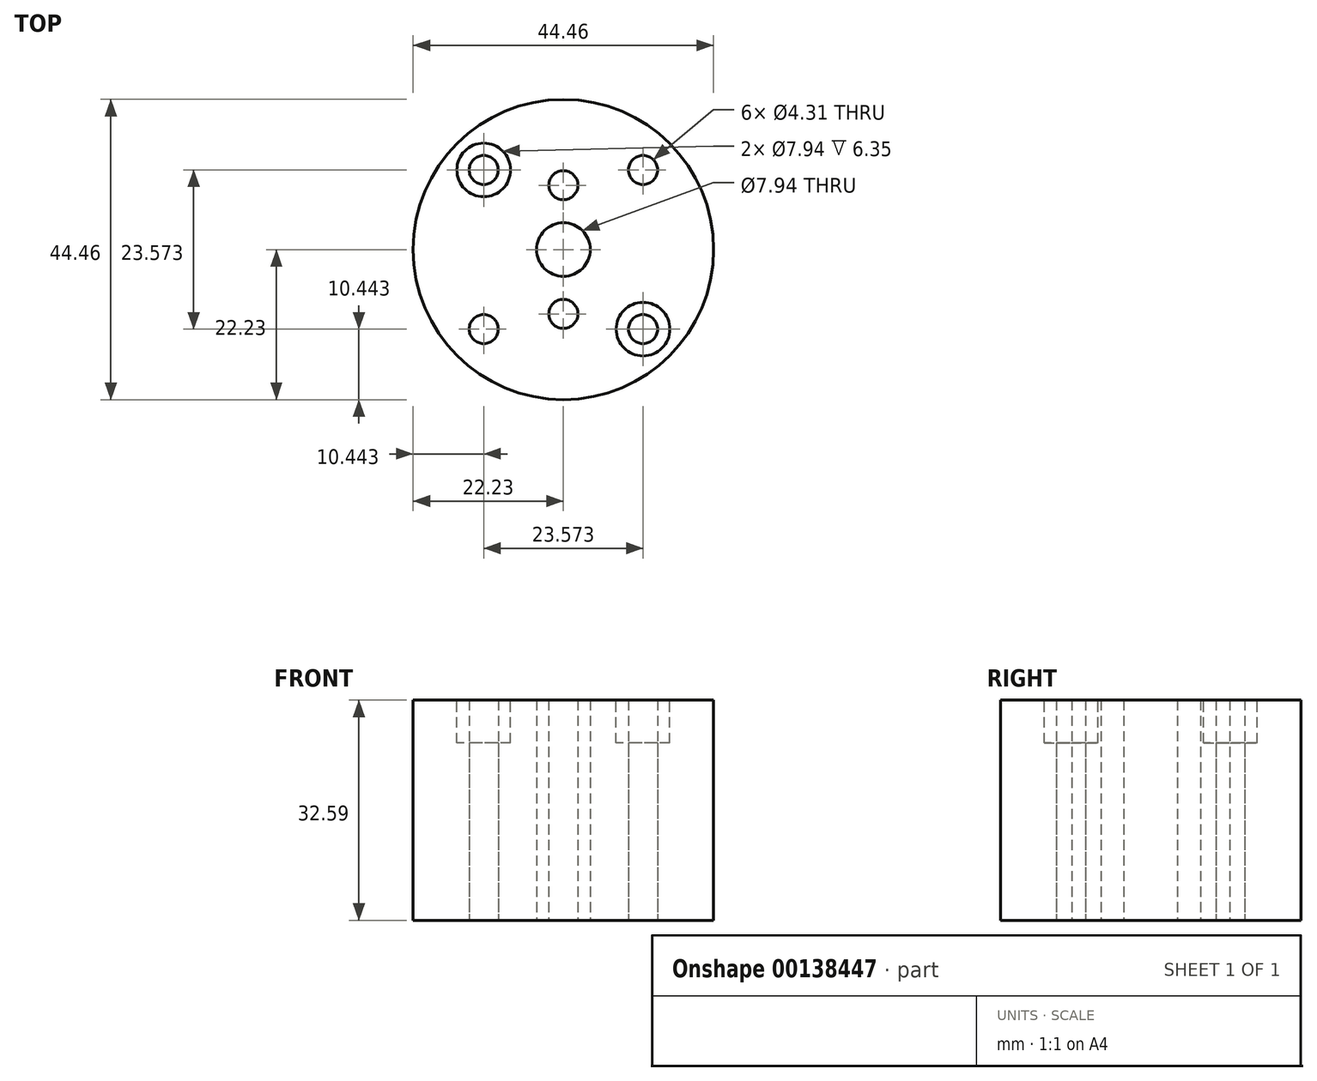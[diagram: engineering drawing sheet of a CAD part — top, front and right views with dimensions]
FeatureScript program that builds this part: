
annotation { "Feature Type Name" : "Feature", "Feature Type Description" : "" }
export const myFeature = defineFeature(function(context is Context, id is Id, definition is map)
    precondition{}
    {
        {
            var Q0;
            Q0=qCreatedBy(makeId("Top.planeOp"),FACE);
            var sketch = newSketch(context, id + "F0", { "sketchPlane" : qUnion([Q0])});
            skCircle(sketch, "E0", {"center": v(0, 0) * mm, "radius": 3.97 * mm});
            skLineSegment(sketch, "E1.bottom", {"start": v(-11.79, 11.79) * mm, "end": v(11.79, 11.79) * mm, "construction": true});
            skLineSegment(sketch, "E1.top", {"start": v(-11.79, -11.79) * mm, "end": v(11.79, -11.79) * mm, "construction": true});
            skLineSegment(sketch, "E1.left", {"start": v(-11.79, 11.79) * mm, "end": v(-11.79, -11.79) * mm, "construction": true});
            skLineSegment(sketch, "E1.right", {"start": v(11.79, 11.79) * mm, "end": v(11.79, -11.79) * mm, "construction": true});
            skCircle(sketch, "E2", {"center": v(0, 0) * mm, "radius": 11.11 * mm, "construction": true});
            skCircle(sketch, "E3", {"center": v(-11.79, 11.79) * mm, "radius": 5.56 * mm, "construction": true});
            skCircle(sketch, "E4", {"center": v(-11.79, 11.79) * mm, "radius": 2.15 * mm});
            skCircle(sketch, "E5", {"center": v(11.79, 11.79) * mm, "radius": 2.15 * mm});
            skCircle(sketch, "E6", {"center": v(-11.79, -11.79) * mm, "radius": 2.15 * mm});
            skCircle(sketch, "E7", {"center": v(11.79, -11.79) * mm, "radius": 2.15 * mm});
            skLineSegment(sketch, "E8", {"start": v(0, 0) * mm, "end": v(22.23, 0) * mm, "construction": true});
            skCircle(sketch, "E9", {"center": v(0, 0) * mm, "radius": 22.22 * mm});
            skLineSegment(sketch, "E10", {"start": v(0, 9.53) * mm, "end": v(0, -9.53) * mm, "construction": true});
            skCircle(sketch, "E11", {"center": v(0, 9.53) * mm, "radius": 5.56 * mm, "construction": true});
            skCircle(sketch, "E12", {"center": v(0, 9.53) * mm, "radius": 2.15 * mm});
            skCircle(sketch, "E13", {"center": v(0, -9.53) * mm, "radius": 2.15 * mm});
            skSolve(sketch);
        }
        {
            var Q0;
            Q0=qSketchRegion(id+"F0",true);
            extrude(context, id + "F1", {"entities" : qUnion([Q0]), "depth" : 32.6 * mm});
        }
        {
            var Q0;
            Q0=makeQuery(id+"F1.opExtrude","CAP_FACE",FACE,{"disambiguationData":[OSD([sQuery(id+"F0.wireOp",EDGE,"E0"),sQuery(id+"F0.wireOp",EDGE,"E4"),sQuery(id+"F0.wireOp",EDGE,"E5"),sQuery(id+"F0.wireOp",EDGE,"E6"),sQuery(id+"F0.wireOp",EDGE,"E7"),sQuery(id+"F0.wireOp",EDGE,"E9")])],"isStart":false});
            var sketch = newSketch(context, id + "F2", { "sketchPlane" : qUnion([Q0])});
            skCircle(sketch, "E14", {"center": v(-11.79, 11.79) * mm, "radius": 3.97 * mm});
            skCircle(sketch, "E15", {"center": v(11.79, -11.79) * mm, "radius": 3.97 * mm});
            skSolve(sketch);
        }
        {
            var Q0;
            Q0 = qSketchRegion(id + "F2", true);
            extrude(context, id + "F3", {"entities" : qUnion([Q0]), "operationType" : NewBodyOperationType.REMOVE, "oppositeDirection" : true, "depth" : 6.35 * mm});
        }
    });
